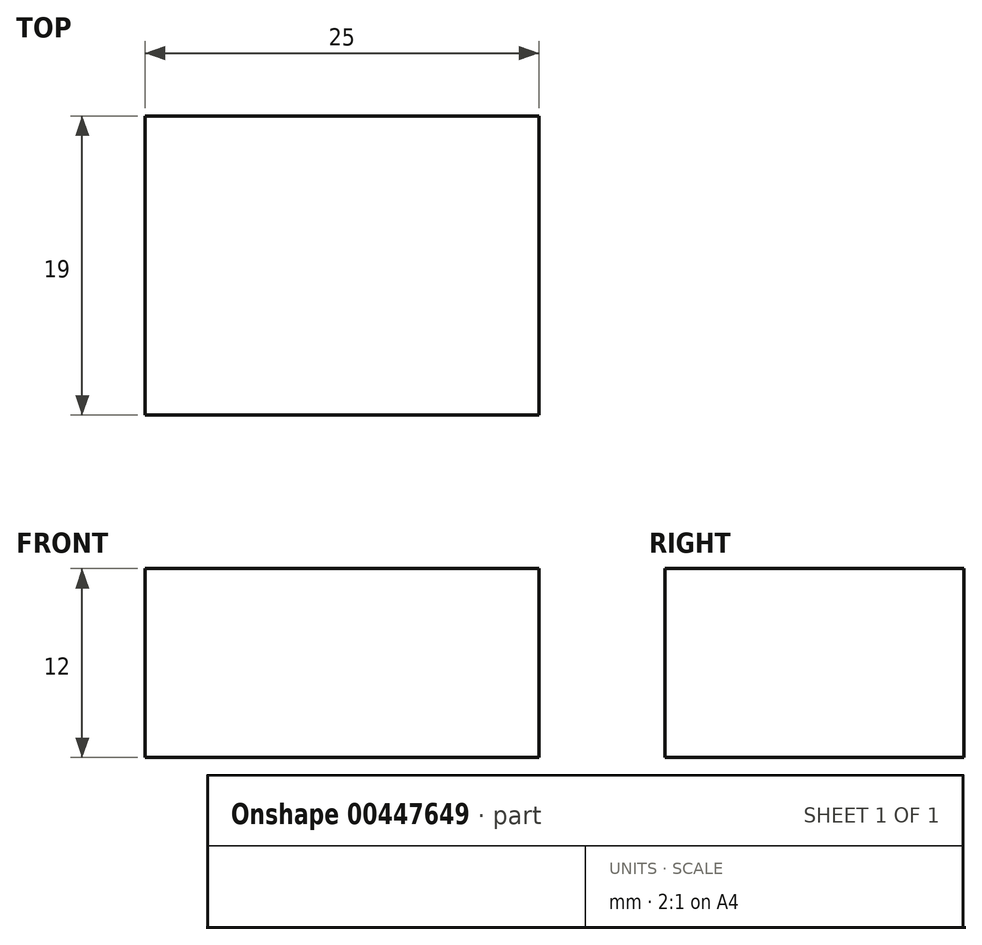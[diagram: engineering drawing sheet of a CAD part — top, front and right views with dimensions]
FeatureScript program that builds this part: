
annotation { "Feature Type Name" : "Feature", "Feature Type Description" : "" }
export const myFeature = defineFeature(function(context is Context, id is Id, definition is map)
    precondition{}
    {
        {
            var Q0;
            Q0=qCreatedBy(makeId("Right.planeOp"),FACE);
            var sketch = newSketch(context, id + "F0", { "sketchPlane" : qUnion([Q0])});
            skLineSegment(sketch, "E0.bottom", {"start": v(9.5, -6) * mm, "end": v(-9.5, -6) * mm});
            skLineSegment(sketch, "E0.top", {"start": v(9.5, 6) * mm, "end": v(-9.5, 6) * mm});
            skLineSegment(sketch, "E0.left", {"start": v(9.5, -6) * mm, "end": v(9.5, 6) * mm});
            skLineSegment(sketch, "E0.right", {"start": v(-9.5, -6) * mm, "end": v(-9.5, 6) * mm});
            skPoint(sketch, "E0.middle", {"position": v(0, 0) * mm});
            skSolve(sketch);
        }
        {
            var Q0;
            Q0=makeQuery(id+"F0.imprint","IMPRINT",FACE,{"disambiguationData":[TD([[makeQuery(id+"F0.imprint","IMPRINT",EDGE,{"derivedFrom":sQuery(id+"F0.wireOp",EDGE,"E0.bottom")}),-1.0]])]});
            extrude(context, id + "F1", {"entities" : qUnion([Q0]), "depth" : 25 * mm});
        }
    });
